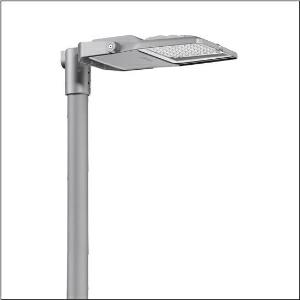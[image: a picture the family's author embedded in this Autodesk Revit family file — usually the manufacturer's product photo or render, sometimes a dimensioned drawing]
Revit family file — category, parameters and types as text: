
# Revit family: floodlight_fl_21_mini___pl64_5xa7775c2e3a_8880
name_source: partatom
category: Lighting Fixtures
units: mm (PartAtom-declared; Revit-internal decimal feet)

## family parameters
Cut with Voids When Loaded = No
Host = Face
Light Source = No
Part Type = Normal
Room Calculation Point = No
Round Connector Dimension = Use Diameter
Shared = No

## types (1)
- --- (1 x LED, 11770 lm, 89 W, 3000K)
    Apparent Load = 89 VA
    CIE Flux Codes = 28 80 98 100 100
    Color Rendering = 70
    Color Temperature = 3000K
    Default Elevation = 1800 mm
    Description = Floodlight FL 21 mini, floodlight, primary light control with lens, of PMMA, primary optical cover: protective disc, of toughened safety glass, transparent, light distribution: PL64, light emission: direct distribution, installation type: surface-mounted, LED, High Power LED, rated luminous flux: 11.770lm, luminous efficacy: 132lm/W, light colour: 730, colour temperature: 3000K, control gear: Smart Interface (Zhaga), control: flexible luminous flux parameterisation, time-dependent luminous flux control, constant luminous flux control, overheat protection, pre-setting: logarithmic dimming characteristic, with terminal, 6-pole, mains connection: 220..240V, AC, 50/60Hz, start of lifetime: 89W, end of service life: 94W, reduction: 43W, luminaire housing, of diecast aluminium, powder-coated, SITECO metallic grey (DB 702S), corrosivity category C5 mid according to DIN EN ISO 12944, suitable for swimming pools, chlorine-resistant, sealing non-destructively replaceable, please order mast flange separately, mast bracket, of steel, galvanised, powder-coated, SITECO metallic grey (DB 702S), Smart Interface above, protection rating (complete): IP66, insulation class (complete): insulation class II (safety insulation), certification: CE, ENEC, VDE, protection symbol: D, impact resistance: IK08, permissible operating ambient temperature: -40..+40°C, permissible operating ambient temperature for outdoor applications: -40..+50°C, standard: DIN EN 12944, LABS conformity tested according to VDMA 24364:2018-05, packaging unit: 1 piece

Light Distribution: PL64
    Height = 70 mm
    Lamp = 1 x LED
    Lamp Light Flux = 11770 lm
    Lamp Power = 89 W
    Lamp count = 1
    Length = 485 mm
    Luminous efficacy = 132 lm/W
    Manufacturer = Siteco
    ModVariant = No
    Model = 5XA7775C2E3A
    Mounting Place = Pole
    Mounting Type = Pole annexe
    Number of Poles = 1
    OnlyDefault = Yes
    Power Factor = 1
    Product Name = Floodlight FL 21 mini | PL64
    Product group = floodlight | pylon annexe
    ProductGroupID = 6201
    Protection Class = Protection class II
    Protection Degree = IP 66
    RLX_Detail_Level = 1
    RLX_Emergency_Light_Flux = 0 lm
    RLX_Emergency_Type = 0
    RLX_Emergency_Type_DB = No
    RlxData = <blob elided: 101041 chars, md5=2a5e55ea>
    Socket = socket
    Standby Power = 0 W
    System Light Flux = 11770 lm
    System Power = 89 W
    Type Comments = factory setting: luminous flux: 100 % | dim-lin: 254 | 456 mA
    Type Image = l_1007125.jpg
    URL = http://relux.com
    VarID = @adj_166441
    Voltage = 0 V
    Weight = 0.00 kg
    Width = 337 mm

## geometry (parser evidence)
native form markers: Blend x4, Sweep x11
no freeform markers — native parametric forms only
